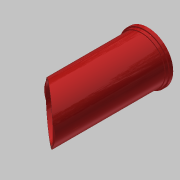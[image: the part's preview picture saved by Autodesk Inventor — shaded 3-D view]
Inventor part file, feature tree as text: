
AUTODESK INVENTOR PART (.ipt)
format: ipt  version: 2017.3 (Build 213257000, 257)  size: 154,624 bytes
history: native  units: in
note: dims shown in document units (in); Inventor stores cm internally (conversion verified against a paired STEP export)
features: extrude x5, sketch x5, fillet x2, chamfer x1
ambient origin geometry x8: Origin, YZ Plane, XZ Plane, XY Plane, X Axis, Y Axis, Z Axis, Center Point
bodies: Solid1 (feature_tree)
feature tree (13):
  extrude  "Extrusion1"  Depth=2.0in TaperAngle=0.0deg
  extrude  "Extrusion2"  Depth=3.75in TaperAngle=0.0deg
  extrude  "Extrusion3"  Depth=68.7402in TaperAngle=0.0deg
  extrude  "Extrusion4"  Depth=0.0312in TaperAngle=0.0deg
  chamfer  "Chamfer1"  Distance=0.0312in Angle=45.0deg
  fillet  "Fillet1"  Radius=0.0312in
  fillet  "Fillet2"  Radius=0.0312in
  extrude  "Extrusion5"  Depth=1.0in TaperAngle=0.0deg
  sketch  "Sketch1"  dims[d0=30.02in d1=2.0in d2=0.0in]
  sketch  "Sketch2"  dims[d3=28.52in d4=3.75in d5=0.0in]
  sketch  "Sketch3"  dims[d6=27.5in d7=68.7402in d8=0.0in]
  sketch  "Sketch4"  dims[d9=25.0in d11=30.9055in d12=0.0in d13=0.0312in d14=0.125in d15=45.0deg d16=0.0312in d17=0.0312in]
  sketch  "Sketch5"  dims[d18=0.2749in d19=1.0in d20=0.0in d24=0.25in]
